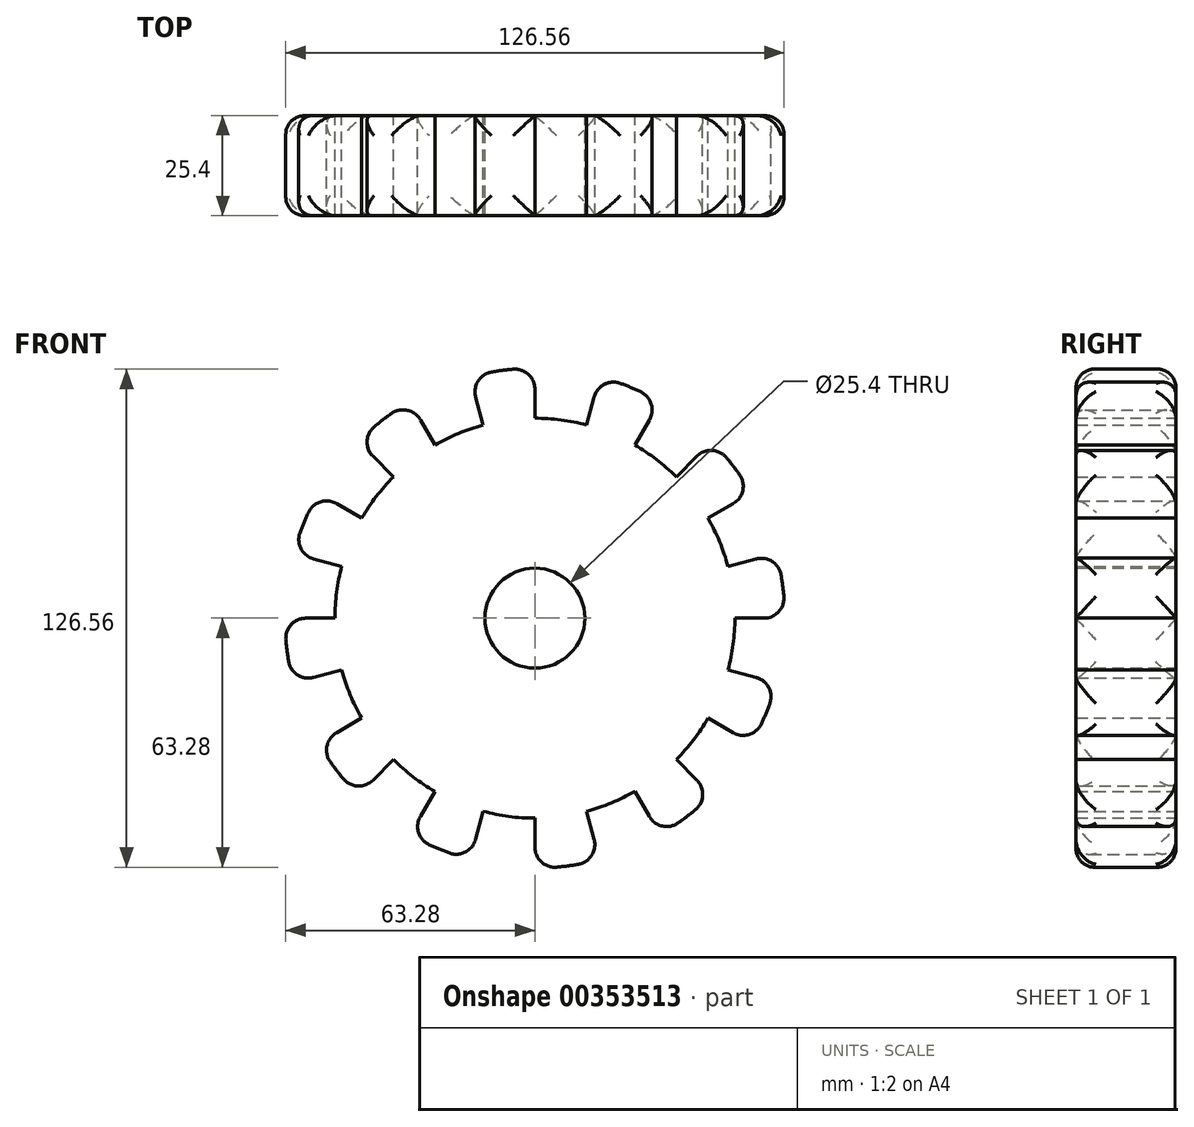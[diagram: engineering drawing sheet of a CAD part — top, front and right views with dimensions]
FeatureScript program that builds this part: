
annotation { "Feature Type Name" : "Feature", "Feature Type Description" : "" }
export const myFeature = defineFeature(function(context is Context, id is Id, definition is map)
    precondition{}
    {
        {
            var Q0;
            Q0=qCreatedBy(makeId("Front.planeOp"),FACE);
            var sketch = newSketch(context, id + "F0", { "sketchPlane" : qUnion([Q0])});
            skCircle(sketch, "E0", {"center": v(0, 0) * mm, "radius": 63.5 * mm});
            skLineSegment(sketch, "E1", {"start": v(0, 0) * mm, "end": v(0, 63.5) * mm});
            skLineSegment(sketch, "E2", {"start": v(0, 0) * mm, "end": v(16.44, 61.34) * mm});
            skLineSegment(sketch, "E3", {"start": v(0, 0) * mm, "end": v(31.75, 55) * mm});
            skLineSegment(sketch, "E4", {"start": v(0, 0) * mm, "end": v(44.9, 44.9) * mm});
            skLineSegment(sketch, "E5", {"start": v(0, 0) * mm, "end": v(55, 31.75) * mm});
            skLineSegment(sketch, "E6", {"start": v(0, 0) * mm, "end": v(61.34, 16.44) * mm});
            skLineSegment(sketch, "E7", {"start": v(0, 0) * mm, "end": v(63.5, 0) * mm});
            skLineSegment(sketch, "E8", {"start": v(0, 0) * mm, "end": v(61.34, -16.44) * mm});
            skLineSegment(sketch, "E9", {"start": v(0, 0) * mm, "end": v(56.33, -32.52) * mm});
            skLineSegment(sketch, "E10", {"start": v(0, 0) * mm, "end": v(44.9, -44.9) * mm});
            skLineSegment(sketch, "E11", {"start": v(0, 0) * mm, "end": v(31.75, -55) * mm});
            skLineSegment(sketch, "E12", {"start": v(0, 0) * mm, "end": v(16.44, -61.34) * mm});
            skLineSegment(sketch, "E13", {"start": v(0, 0) * mm, "end": v(0, -63.5) * mm});
            skLineSegment(sketch, "E14", {"start": v(0, 0) * mm, "end": v(-16.44, -61.34) * mm});
            skLineSegment(sketch, "E15", {"start": v(0, 0) * mm, "end": v(-31.75, -55) * mm});
            skLineSegment(sketch, "E16", {"start": v(0, 0) * mm, "end": v(-44.9, -44.9) * mm});
            skLineSegment(sketch, "E17", {"start": v(0, 0) * mm, "end": v(-56.8, -32.8) * mm});
            skLineSegment(sketch, "E18", {"start": v(0, 0) * mm, "end": v(-61.34, -16.44) * mm});
            skLineSegment(sketch, "E19", {"start": v(0, 0) * mm, "end": v(-61.34, 16.44) * mm});
            skLineSegment(sketch, "E20", {"start": v(0, 0) * mm, "end": v(-55, 31.75) * mm});
            skLineSegment(sketch, "E21", {"start": v(0, 0) * mm, "end": v(-44.9, 44.9) * mm});
            skLineSegment(sketch, "E22", {"start": v(0, 0) * mm, "end": v(-31.75, 55) * mm});
            skLineSegment(sketch, "E23", {"start": v(0, 0) * mm, "end": v(-16.44, 61.34) * mm});
            skLineSegment(sketch, "E24", {"start": v(0, 0) * mm, "end": v(-63.5, 0) * mm});
            skCircle(sketch, "E25", {"center": v(0, 0) * mm, "radius": 50.8 * mm});
            skCircle(sketch, "E26", {"center": v(0, 0) * mm, "radius": 12.7 * mm});
            skSolve(sketch);
        }
        {
            var Q0;
            {var subQ0=sQuery(id+"F0.wireOp",EDGE,"E19");var subQ1=sQuery(id+"F0.wireOp",EDGE,"E0");var subQ2=makeQuery(id+"F0.imprint","INTERSECT",VERTEX,{"derivedFrom":[subQ1,subQ0]});Q0=makeQuery(id+"F0.imprint","IMPRINT",FACE,{"disambiguationData":[TD([[makeQuery(id+"F0.imprint","IMPRINT",EDGE,{"disambiguationData":[TD([[subQ2,1.0]])],"derivedFrom":subQ1}),1.0]])]});}
            var Q1;
            {var subQ0=sQuery(id+"F0.wireOp",EDGE,"E23");var subQ1=sQuery(id+"F0.wireOp",EDGE,"E0");var subQ2=makeQuery(id+"F0.imprint","INTERSECT",VERTEX,{"derivedFrom":[subQ1,subQ0]});Q1=makeQuery(id+"F0.imprint","IMPRINT",FACE,{"disambiguationData":[TD([[makeQuery(id+"F0.imprint","IMPRINT",EDGE,{"disambiguationData":[TD([[subQ2,1.0]])],"derivedFrom":subQ1}),1.0]])]});}
            var Q2;
            {var subQ1=sQuery(id+"F0.wireOp",EDGE,"E2");var subQ3=sQuery(id+"F0.wireOp",EDGE,"E25");var subQ4=makeQuery(id+"F0.imprint","INTERSECT",VERTEX,{"derivedFrom":[subQ1,subQ3]});Q2=makeQuery(id+"F0.imprint","IMPRINT",FACE,{"disambiguationData":[TD([[makeQuery(id+"F0.imprint","IMPRINT",EDGE,{"disambiguationData":[TD([[subQ4,1.0]])],"derivedFrom":subQ3}),1.0]])]});}
            var Q3;
            {var subQ1=sQuery(id+"F0.wireOp",EDGE,"E8");var subQ3=sQuery(id+"F0.wireOp",EDGE,"E25");var subQ4=makeQuery(id+"F0.imprint","INTERSECT",VERTEX,{"derivedFrom":[subQ1,subQ3]});Q3=makeQuery(id+"F0.imprint","IMPRINT",FACE,{"disambiguationData":[TD([[makeQuery(id+"F0.imprint","IMPRINT",EDGE,{"disambiguationData":[TD([[subQ4,1.0]])],"derivedFrom":subQ3}),1.0]])]});}
            var Q4;
            {var subQ1=sQuery(id+"F0.wireOp",EDGE,"E10");var subQ3=sQuery(id+"F0.wireOp",EDGE,"E25");var subQ4=makeQuery(id+"F0.imprint","INTERSECT",VERTEX,{"derivedFrom":[subQ1,subQ3]});Q4=makeQuery(id+"F0.imprint","IMPRINT",FACE,{"disambiguationData":[TD([[makeQuery(id+"F0.imprint","IMPRINT",EDGE,{"disambiguationData":[TD([[subQ4,1.0]])],"derivedFrom":subQ3}),1.0]])]});}
            var Q5;
            {var subQ1=sQuery(id+"F0.wireOp",EDGE,"E12");var subQ3=sQuery(id+"F0.wireOp",EDGE,"E25");var subQ4=makeQuery(id+"F0.imprint","INTERSECT",VERTEX,{"derivedFrom":[subQ1,subQ3]});Q5=makeQuery(id+"F0.imprint","IMPRINT",FACE,{"disambiguationData":[TD([[makeQuery(id+"F0.imprint","IMPRINT",EDGE,{"disambiguationData":[TD([[subQ4,1.0]])],"derivedFrom":subQ3}),1.0]])]});}
            var Q6;
            {var subQ1=sQuery(id+"F0.wireOp",EDGE,"E14");var subQ3=sQuery(id+"F0.wireOp",EDGE,"E25");var subQ4=makeQuery(id+"F0.imprint","INTERSECT",VERTEX,{"derivedFrom":[subQ1,subQ3]});Q6=makeQuery(id+"F0.imprint","IMPRINT",FACE,{"disambiguationData":[TD([[makeQuery(id+"F0.imprint","IMPRINT",EDGE,{"disambiguationData":[TD([[subQ4,1.0]])],"derivedFrom":subQ3}),1.0]])]});}
            var Q7;
            {var subQ1=sQuery(id+"F0.wireOp",EDGE,"E16");var subQ3=sQuery(id+"F0.wireOp",EDGE,"E25");var subQ4=makeQuery(id+"F0.imprint","INTERSECT",VERTEX,{"derivedFrom":[subQ1,subQ3]});Q7=makeQuery(id+"F0.imprint","IMPRINT",FACE,{"disambiguationData":[TD([[makeQuery(id+"F0.imprint","IMPRINT",EDGE,{"disambiguationData":[TD([[subQ4,1.0]])],"derivedFrom":subQ3}),1.0]])]});}
            var Q8;
            {var subQ1=sQuery(id+"F0.wireOp",EDGE,"E18");var subQ3=sQuery(id+"F0.wireOp",EDGE,"E25");var subQ4=makeQuery(id+"F0.imprint","INTERSECT",VERTEX,{"derivedFrom":[subQ1,subQ3]});Q8=makeQuery(id+"F0.imprint","IMPRINT",FACE,{"disambiguationData":[TD([[makeQuery(id+"F0.imprint","IMPRINT",EDGE,{"disambiguationData":[TD([[subQ4,1.0]])],"derivedFrom":subQ3}),1.0]])]});}
            var Q9;
            {var subQ0=sQuery(id+"F0.wireOp",EDGE,"E21");var subQ1=sQuery(id+"F0.wireOp",EDGE,"E0");var subQ2=makeQuery(id+"F0.imprint","INTERSECT",VERTEX,{"derivedFrom":[subQ1,subQ0]});Q9=makeQuery(id+"F0.imprint","IMPRINT",FACE,{"disambiguationData":[TD([[makeQuery(id+"F0.imprint","IMPRINT",EDGE,{"disambiguationData":[TD([[subQ2,1.0]])],"derivedFrom":subQ1}),1.0]])]});}
            var Q10;
            {var subQ0=sQuery(id+"F0.wireOp",EDGE,"E2");var subQ1=sQuery(id+"F0.wireOp",EDGE,"E0");var subQ2=makeQuery(id+"F0.imprint","INTERSECT",VERTEX,{"derivedFrom":[subQ1,subQ0]});Q10=makeQuery(id+"F0.imprint","IMPRINT",FACE,{"disambiguationData":[TD([[makeQuery(id+"F0.imprint","IMPRINT",EDGE,{"disambiguationData":[TD([[subQ2,1.0]])],"derivedFrom":subQ1}),1.0]])]});}
            var Q11;
            {var subQ0=sQuery(id+"F0.wireOp",EDGE,"E4");var subQ1=sQuery(id+"F0.wireOp",EDGE,"E0");var subQ2=makeQuery(id+"F0.imprint","INTERSECT",VERTEX,{"derivedFrom":[subQ1,subQ0]});Q11=makeQuery(id+"F0.imprint","IMPRINT",FACE,{"disambiguationData":[TD([[makeQuery(id+"F0.imprint","IMPRINT",EDGE,{"disambiguationData":[TD([[subQ2,1.0]])],"derivedFrom":subQ1}),1.0]])]});}
            var Q12;
            {var subQ0=sQuery(id+"F0.wireOp",EDGE,"E6");var subQ1=sQuery(id+"F0.wireOp",EDGE,"E0");var subQ2=makeQuery(id+"F0.imprint","INTERSECT",VERTEX,{"derivedFrom":[subQ1,subQ0]});Q12=makeQuery(id+"F0.imprint","IMPRINT",FACE,{"disambiguationData":[TD([[makeQuery(id+"F0.imprint","IMPRINT",EDGE,{"disambiguationData":[TD([[subQ2,1.0]])],"derivedFrom":subQ1}),1.0]])]});}
            var Q13;
            {var subQ0=sQuery(id+"F0.wireOp",EDGE,"E8");var subQ1=sQuery(id+"F0.wireOp",EDGE,"E0");var subQ2=makeQuery(id+"F0.imprint","INTERSECT",VERTEX,{"derivedFrom":[subQ1,subQ0]});Q13=makeQuery(id+"F0.imprint","IMPRINT",FACE,{"disambiguationData":[TD([[makeQuery(id+"F0.imprint","IMPRINT",EDGE,{"disambiguationData":[TD([[subQ2,1.0]])],"derivedFrom":subQ1}),1.0]])]});}
            var Q14;
            {var subQ0=sQuery(id+"F0.wireOp",EDGE,"E10");var subQ1=sQuery(id+"F0.wireOp",EDGE,"E0");var subQ2=makeQuery(id+"F0.imprint","INTERSECT",VERTEX,{"derivedFrom":[subQ1,subQ0]});Q14=makeQuery(id+"F0.imprint","IMPRINT",FACE,{"disambiguationData":[TD([[makeQuery(id+"F0.imprint","IMPRINT",EDGE,{"disambiguationData":[TD([[subQ2,1.0]])],"derivedFrom":subQ1}),1.0]])]});}
            var Q15;
            {var subQ0=sQuery(id+"F0.wireOp",EDGE,"E12");var subQ1=sQuery(id+"F0.wireOp",EDGE,"E0");var subQ2=makeQuery(id+"F0.imprint","INTERSECT",VERTEX,{"derivedFrom":[subQ1,subQ0]});Q15=makeQuery(id+"F0.imprint","IMPRINT",FACE,{"disambiguationData":[TD([[makeQuery(id+"F0.imprint","IMPRINT",EDGE,{"disambiguationData":[TD([[subQ2,1.0]])],"derivedFrom":subQ1}),1.0]])]});}
            var Q16;
            {var subQ0=sQuery(id+"F0.wireOp",EDGE,"E14");var subQ1=sQuery(id+"F0.wireOp",EDGE,"E0");var subQ2=makeQuery(id+"F0.imprint","INTERSECT",VERTEX,{"derivedFrom":[subQ1,subQ0]});Q16=makeQuery(id+"F0.imprint","IMPRINT",FACE,{"disambiguationData":[TD([[makeQuery(id+"F0.imprint","IMPRINT",EDGE,{"disambiguationData":[TD([[subQ2,1.0]])],"derivedFrom":subQ1}),1.0]])]});}
            var Q17;
            {var subQ0=sQuery(id+"F0.wireOp",EDGE,"E16");var subQ1=sQuery(id+"F0.wireOp",EDGE,"E0");var subQ2=makeQuery(id+"F0.imprint","INTERSECT",VERTEX,{"derivedFrom":[subQ1,subQ0]});Q17=makeQuery(id+"F0.imprint","IMPRINT",FACE,{"disambiguationData":[TD([[makeQuery(id+"F0.imprint","IMPRINT",EDGE,{"disambiguationData":[TD([[subQ2,1.0]])],"derivedFrom":subQ1}),1.0]])]});}
            var Q18;
            {var subQ0=sQuery(id+"F0.wireOp",EDGE,"E18");var subQ1=sQuery(id+"F0.wireOp",EDGE,"E0");var subQ2=makeQuery(id+"F0.imprint","INTERSECT",VERTEX,{"derivedFrom":[subQ1,subQ0]});Q18=makeQuery(id+"F0.imprint","IMPRINT",FACE,{"disambiguationData":[TD([[makeQuery(id+"F0.imprint","IMPRINT",EDGE,{"disambiguationData":[TD([[subQ2,1.0]])],"derivedFrom":subQ1}),1.0]])]});}
            var Q19;
            {var subQ1=sQuery(id+"F0.wireOp",EDGE,"E19");var subQ3=sQuery(id+"F0.wireOp",EDGE,"E25");var subQ4=makeQuery(id+"F0.imprint","INTERSECT",VERTEX,{"derivedFrom":[subQ1,subQ3]});Q19=makeQuery(id+"F0.imprint","IMPRINT",FACE,{"disambiguationData":[TD([[makeQuery(id+"F0.imprint","IMPRINT",EDGE,{"disambiguationData":[TD([[subQ4,1.0]])],"derivedFrom":subQ3}),1.0]])]});}
            var Q20;
            {var subQ1=sQuery(id+"F0.wireOp",EDGE,"E21");var subQ3=sQuery(id+"F0.wireOp",EDGE,"E25");var subQ4=makeQuery(id+"F0.imprint","INTERSECT",VERTEX,{"derivedFrom":[subQ1,subQ3]});Q20=makeQuery(id+"F0.imprint","IMPRINT",FACE,{"disambiguationData":[TD([[makeQuery(id+"F0.imprint","IMPRINT",EDGE,{"disambiguationData":[TD([[subQ4,1.0]])],"derivedFrom":subQ3}),1.0]])]});}
            var Q21;
            {var subQ1=sQuery(id+"F0.wireOp",EDGE,"E23");var subQ3=sQuery(id+"F0.wireOp",EDGE,"E25");var subQ4=makeQuery(id+"F0.imprint","INTERSECT",VERTEX,{"derivedFrom":[subQ1,subQ3]});Q21=makeQuery(id+"F0.imprint","IMPRINT",FACE,{"disambiguationData":[TD([[makeQuery(id+"F0.imprint","IMPRINT",EDGE,{"disambiguationData":[TD([[subQ4,1.0]])],"derivedFrom":subQ3}),1.0]])]});}
            var Q22;
            {var subQ1=sQuery(id+"F0.wireOp",EDGE,"E4");var subQ3=sQuery(id+"F0.wireOp",EDGE,"E25");var subQ4=makeQuery(id+"F0.imprint","INTERSECT",VERTEX,{"derivedFrom":[subQ1,subQ3]});Q22=makeQuery(id+"F0.imprint","IMPRINT",FACE,{"disambiguationData":[TD([[makeQuery(id+"F0.imprint","IMPRINT",EDGE,{"disambiguationData":[TD([[subQ4,1.0]])],"derivedFrom":subQ3}),1.0]])]});}
            var Q23;
            {var subQ1=sQuery(id+"F0.wireOp",EDGE,"E6");var subQ3=sQuery(id+"F0.wireOp",EDGE,"E25");var subQ4=makeQuery(id+"F0.imprint","INTERSECT",VERTEX,{"derivedFrom":[subQ1,subQ3]});Q23=makeQuery(id+"F0.imprint","IMPRINT",FACE,{"disambiguationData":[TD([[makeQuery(id+"F0.imprint","IMPRINT",EDGE,{"disambiguationData":[TD([[subQ4,1.0]])],"derivedFrom":subQ3}),1.0]])]});}
            var Q24;
            {var subQ1=sQuery(id+"F0.wireOp",EDGE,"E7");var subQ3=sQuery(id+"F0.wireOp",EDGE,"E25");var subQ4=makeQuery(id+"F0.imprint","INTERSECT",VERTEX,{"derivedFrom":[subQ1,subQ3]});Q24=makeQuery(id+"F0.imprint","IMPRINT",FACE,{"disambiguationData":[TD([[makeQuery(id+"F0.imprint","IMPRINT",EDGE,{"disambiguationData":[TD([[subQ4,1.0]])],"derivedFrom":subQ3}),1.0]])]});}
            var Q25;
            {var subQ1=sQuery(id+"F0.wireOp",EDGE,"E9");var subQ3=sQuery(id+"F0.wireOp",EDGE,"E25");var subQ4=makeQuery(id+"F0.imprint","INTERSECT",VERTEX,{"derivedFrom":[subQ1,subQ3]});Q25=makeQuery(id+"F0.imprint","IMPRINT",FACE,{"disambiguationData":[TD([[makeQuery(id+"F0.imprint","IMPRINT",EDGE,{"disambiguationData":[TD([[subQ4,1.0]])],"derivedFrom":subQ3}),1.0]])]});}
            var Q26;
            {var subQ1=sQuery(id+"F0.wireOp",EDGE,"E11");var subQ3=sQuery(id+"F0.wireOp",EDGE,"E25");var subQ4=makeQuery(id+"F0.imprint","INTERSECT",VERTEX,{"derivedFrom":[subQ1,subQ3]});Q26=makeQuery(id+"F0.imprint","IMPRINT",FACE,{"disambiguationData":[TD([[makeQuery(id+"F0.imprint","IMPRINT",EDGE,{"disambiguationData":[TD([[subQ4,1.0]])],"derivedFrom":subQ3}),1.0]])]});}
            var Q27;
            {var subQ1=sQuery(id+"F0.wireOp",EDGE,"E13");var subQ3=sQuery(id+"F0.wireOp",EDGE,"E25");var subQ4=makeQuery(id+"F0.imprint","INTERSECT",VERTEX,{"derivedFrom":[subQ1,subQ3]});Q27=makeQuery(id+"F0.imprint","IMPRINT",FACE,{"disambiguationData":[TD([[makeQuery(id+"F0.imprint","IMPRINT",EDGE,{"disambiguationData":[TD([[subQ4,1.0]])],"derivedFrom":subQ3}),1.0]])]});}
            var Q28;
            {var subQ1=sQuery(id+"F0.wireOp",EDGE,"E15");var subQ3=sQuery(id+"F0.wireOp",EDGE,"E25");var subQ4=makeQuery(id+"F0.imprint","INTERSECT",VERTEX,{"derivedFrom":[subQ1,subQ3]});Q28=makeQuery(id+"F0.imprint","IMPRINT",FACE,{"disambiguationData":[TD([[makeQuery(id+"F0.imprint","IMPRINT",EDGE,{"disambiguationData":[TD([[subQ4,1.0]])],"derivedFrom":subQ3}),1.0]])]});}
            var Q29;
            Q29=makeQuery(id+"FHpyQ5VTINkMJPX_0.imprint","IMPRINT",FACE,{"disambiguationData":[TD([[makeQuery(id+"FHpyQ5VTINkMJPX_0.imprint","IMPRINT",EDGE,{"derivedFrom":sQuery(id+"FHpyQ5VTINkMJPX_0.wireOp",EDGE,"8gVisn6h-QOQK-Ooiz-TC9m-HFAmxrKovwxp")}),1.0]])]});
            var Q30;
            {var subQ1=sQuery(id+"F0.wireOp",EDGE,"E17");var subQ3=sQuery(id+"F0.wireOp",EDGE,"E25");var subQ4=makeQuery(id+"F0.imprint","INTERSECT",VERTEX,{"derivedFrom":[subQ1,subQ3]});Q30=makeQuery(id+"F0.imprint","IMPRINT",FACE,{"disambiguationData":[TD([[makeQuery(id+"F0.imprint","IMPRINT",EDGE,{"disambiguationData":[TD([[subQ4,1.0]])],"derivedFrom":subQ3}),1.0]])]});}
            var Q31;
            {var subQ1=sQuery(id+"F0.wireOp",EDGE,"E19");var subQ3=sQuery(id+"F0.wireOp",EDGE,"E25");var subQ4=makeQuery(id+"F0.imprint","INTERSECT",VERTEX,{"derivedFrom":[subQ1,subQ3]});Q31=makeQuery(id+"F0.imprint","IMPRINT",FACE,{"disambiguationData":[TD([[makeQuery(id+"F0.imprint","IMPRINT",EDGE,{"disambiguationData":[TD([[subQ4,-1.0]])],"derivedFrom":subQ3}),1.0]])]});}
            var Q32;
            {var subQ1=sQuery(id+"F0.wireOp",EDGE,"E20");var subQ3=sQuery(id+"F0.wireOp",EDGE,"E25");var subQ4=makeQuery(id+"F0.imprint","INTERSECT",VERTEX,{"derivedFrom":[subQ1,subQ3]});Q32=makeQuery(id+"F0.imprint","IMPRINT",FACE,{"disambiguationData":[TD([[makeQuery(id+"F0.imprint","IMPRINT",EDGE,{"disambiguationData":[TD([[subQ4,1.0]])],"derivedFrom":subQ3}),1.0]])]});}
            var Q33;
            {var subQ1=sQuery(id+"F0.wireOp",EDGE,"E22");var subQ3=sQuery(id+"F0.wireOp",EDGE,"E25");var subQ4=makeQuery(id+"F0.imprint","INTERSECT",VERTEX,{"derivedFrom":[subQ1,subQ3]});Q33=makeQuery(id+"F0.imprint","IMPRINT",FACE,{"disambiguationData":[TD([[makeQuery(id+"F0.imprint","IMPRINT",EDGE,{"disambiguationData":[TD([[subQ4,1.0]])],"derivedFrom":subQ3}),1.0]])]});}
            var Q34;
            {var subQ1=sQuery(id+"F0.wireOp",EDGE,"E2");var subQ3=sQuery(id+"F0.wireOp",EDGE,"E25");var subQ4=makeQuery(id+"F0.imprint","INTERSECT",VERTEX,{"derivedFrom":[subQ1,subQ3]});Q34=makeQuery(id+"F0.imprint","IMPRINT",FACE,{"disambiguationData":[TD([[makeQuery(id+"F0.imprint","IMPRINT",EDGE,{"disambiguationData":[TD([[subQ4,-1.0]])],"derivedFrom":subQ3}),1.0]])]});}
            var Q35;
            {var subQ1=sQuery(id+"F0.wireOp",EDGE,"E3");var subQ3=sQuery(id+"F0.wireOp",EDGE,"E25");var subQ4=makeQuery(id+"F0.imprint","INTERSECT",VERTEX,{"derivedFrom":[subQ1,subQ3]});Q35=makeQuery(id+"F0.imprint","IMPRINT",FACE,{"disambiguationData":[TD([[makeQuery(id+"F0.imprint","IMPRINT",EDGE,{"disambiguationData":[TD([[subQ4,1.0]])],"derivedFrom":subQ3}),1.0]])]});}
            var Q36;
            {var subQ1=sQuery(id+"F0.wireOp",EDGE,"E5");var subQ3=sQuery(id+"F0.wireOp",EDGE,"E25");var subQ4=makeQuery(id+"F0.imprint","INTERSECT",VERTEX,{"derivedFrom":[subQ1,subQ3]});Q36=makeQuery(id+"F0.imprint","IMPRINT",FACE,{"disambiguationData":[TD([[makeQuery(id+"F0.imprint","IMPRINT",EDGE,{"disambiguationData":[TD([[subQ4,1.0]])],"derivedFrom":subQ3}),1.0]])]});}
            extrude(context, id + "F1", {"entities" : qUnion([Q0, Q1, Q2, Q3, Q4, Q5, Q6, Q7, Q8, Q9, Q10, Q11, Q12, Q13, Q14, Q15, Q16, Q17, Q18, Q19, Q20, Q21, Q22, Q23, Q24, Q25, Q26, Q27, Q28, Q29, Q30, Q31, Q32, Q33, Q34, Q35, Q36]), "depth" : 25.4 * mm});
        }
        {
            var Q0;
            {var subQ0=sQuery(id+"F0.wireOp",EDGE,"E0");Q0=makeQuery(id+"F1.opExtrude","SWEPT_FACE",FACE,{"disambiguationData":[OSD([subQ0]),TDD([makeQuery(id+"F0.imprint","IMPRINT",EDGE,{"disambiguationData":[TD([[makeQuery(id+"F0.imprint","INTERSECT",VERTEX,{"derivedFrom":[subQ0,sQuery(id+"F0.wireOp",EDGE,"E21")]}),1.0]])],"derivedFrom":subQ0})])]});}
            var Q1;
            {var subQ0=sQuery(id+"F0.wireOp",EDGE,"E0");Q1=makeQuery(id+"F1.opExtrude","SWEPT_FACE",FACE,{"disambiguationData":[OSD([subQ0]),TDD([makeQuery(id+"F0.imprint","IMPRINT",EDGE,{"disambiguationData":[TD([[makeQuery(id+"F0.imprint","INTERSECT",VERTEX,{"derivedFrom":[subQ0,sQuery(id+"F0.wireOp",EDGE,"E19")]}),1.0]])],"derivedFrom":subQ0})])]});}
            var Q2;
            {var subQ0=sQuery(id+"F0.wireOp",EDGE,"E0");Q2=makeQuery(id+"F1.opExtrude","SWEPT_FACE",FACE,{"disambiguationData":[OSD([subQ0]),TDD([makeQuery(id+"F0.imprint","IMPRINT",EDGE,{"disambiguationData":[TD([[makeQuery(id+"F0.imprint","INTERSECT",VERTEX,{"derivedFrom":[subQ0,sQuery(id+"F0.wireOp",EDGE,"E18")]}),1.0]])],"derivedFrom":subQ0})])]});}
            fillet(context, id + "F2", {"entities" : qUnion([Q0, Q1, Q2]), "radius" : 5.08 * mm, "tangentPropagation" : true, "allowEdgeOverflow" : false});
        }
        {
            var Q0;
            {var subQ0=sQuery(id+"F0.wireOp",EDGE,"E0");Q0=makeQuery(id+"F1.opExtrude","SWEPT_FACE",FACE,{"disambiguationData":[OSD([subQ0]),TDD([makeQuery(id+"F0.imprint","IMPRINT",EDGE,{"disambiguationData":[TD([[makeQuery(id+"F0.imprint","INTERSECT",VERTEX,{"derivedFrom":[subQ0,sQuery(id+"F0.wireOp",EDGE,"E23")]}),1.0]])],"derivedFrom":subQ0})])]});}
            var Q1;
            {var subQ0=sQuery(id+"F0.wireOp",EDGE,"E0");Q1=makeQuery(id+"F1.opExtrude","SWEPT_FACE",FACE,{"disambiguationData":[OSD([subQ0]),TDD([makeQuery(id+"F0.imprint","IMPRINT",EDGE,{"disambiguationData":[TD([[makeQuery(id+"F0.imprint","INTERSECT",VERTEX,{"derivedFrom":[subQ0,sQuery(id+"F0.wireOp",EDGE,"E2")]}),1.0]])],"derivedFrom":subQ0})])]});}
            var Q2;
            {var subQ0=sQuery(id+"F0.wireOp",EDGE,"E0");Q2=makeQuery(id+"F1.opExtrude","SWEPT_FACE",FACE,{"disambiguationData":[OSD([subQ0]),TDD([makeQuery(id+"F0.imprint","IMPRINT",EDGE,{"disambiguationData":[TD([[makeQuery(id+"F0.imprint","INTERSECT",VERTEX,{"derivedFrom":[subQ0,sQuery(id+"F0.wireOp",EDGE,"E4")]}),1.0]])],"derivedFrom":subQ0})])]});}
            var Q3;
            {var subQ0=sQuery(id+"F0.wireOp",EDGE,"E0");Q3=makeQuery(id+"F1.opExtrude","SWEPT_FACE",FACE,{"disambiguationData":[OSD([subQ0]),TDD([makeQuery(id+"F0.imprint","IMPRINT",EDGE,{"disambiguationData":[TD([[makeQuery(id+"F0.imprint","INTERSECT",VERTEX,{"derivedFrom":[subQ0,sQuery(id+"F0.wireOp",EDGE,"E6")]}),1.0]])],"derivedFrom":subQ0})])]});}
            var Q4;
            {var subQ0=sQuery(id+"F0.wireOp",EDGE,"E0");Q4=makeQuery(id+"F1.opExtrude","SWEPT_FACE",FACE,{"disambiguationData":[OSD([subQ0]),TDD([makeQuery(id+"F0.imprint","IMPRINT",EDGE,{"disambiguationData":[TD([[makeQuery(id+"F0.imprint","INTERSECT",VERTEX,{"derivedFrom":[subQ0,sQuery(id+"F0.wireOp",EDGE,"E8")]}),1.0]])],"derivedFrom":subQ0})])]});}
            var Q5;
            {var subQ0=sQuery(id+"F0.wireOp",EDGE,"E0");Q5=makeQuery(id+"F1.opExtrude","SWEPT_FACE",FACE,{"disambiguationData":[OSD([subQ0]),TDD([makeQuery(id+"F0.imprint","IMPRINT",EDGE,{"disambiguationData":[TD([[makeQuery(id+"F0.imprint","INTERSECT",VERTEX,{"derivedFrom":[subQ0,sQuery(id+"F0.wireOp",EDGE,"E10")]}),1.0]])],"derivedFrom":subQ0})])]});}
            var Q6;
            Q6=makeQuery(id+"F1.opExtrude","SWEPT_EDGE",EDGE,{"disambiguationData":[OSD([sQuery(id+"F0.wireOp",EDGE,"E0"),sQuery(id+"F0.wireOp",EDGE,"E13")])]});
            var Q7;
            {var subQ0=sQuery(id+"F0.wireOp",EDGE,"E0");Q7=makeQuery(id+"F1.opExtrude","CAP_EDGE",EDGE,{"disambiguationData":[OSD([subQ0]),TDD([makeQuery(id+"F0.imprint","IMPRINT",EDGE,{"disambiguationData":[TD([[makeQuery(id+"F0.imprint","INTERSECT",VERTEX,{"derivedFrom":[subQ0,sQuery(id+"F0.wireOp",EDGE,"E12")]}),1.0]])],"derivedFrom":subQ0})])],"isStart":true});}
            var Q8;
            {var subQ0=sQuery(id+"F0.wireOp",EDGE,"E0");Q8=makeQuery(id+"F1.opExtrude","SWEPT_FACE",FACE,{"disambiguationData":[OSD([subQ0]),TDD([makeQuery(id+"F0.imprint","IMPRINT",EDGE,{"disambiguationData":[TD([[makeQuery(id+"F0.imprint","INTERSECT",VERTEX,{"derivedFrom":[subQ0,sQuery(id+"F0.wireOp",EDGE,"E14")]}),1.0]])],"derivedFrom":subQ0})])]});}
            var Q9;
            {var subQ0=sQuery(id+"F0.wireOp",EDGE,"E0");Q9=makeQuery(id+"F1.opExtrude","SWEPT_FACE",FACE,{"disambiguationData":[OSD([subQ0]),TDD([makeQuery(id+"F0.imprint","IMPRINT",EDGE,{"disambiguationData":[TD([[makeQuery(id+"F0.imprint","INTERSECT",VERTEX,{"derivedFrom":[subQ0,sQuery(id+"F0.wireOp",EDGE,"E16")]}),1.0]])],"derivedFrom":subQ0})])]});}
            var Q10;
            {var subQ0=sQuery(id+"F0.wireOp",EDGE,"E0");Q10=makeQuery(id+"F1.opExtrude","SWEPT_FACE",FACE,{"disambiguationData":[OSD([subQ0]),TDD([makeQuery(id+"F0.imprint","IMPRINT",EDGE,{"disambiguationData":[TD([[makeQuery(id+"F0.imprint","INTERSECT",VERTEX,{"derivedFrom":[subQ0,sQuery(id+"F0.wireOp",EDGE,"E12")]}),1.0]])],"derivedFrom":subQ0})])]});}
            fillet(context, id + "F3", {"entities" : qUnion([Q0, Q1, Q2, Q3, Q4, Q5, Q6, Q7, Q8, Q9, Q10]), "radius" : 5.08 * mm, "tangentPropagation" : true, "allowEdgeOverflow" : false});
        }
    });
